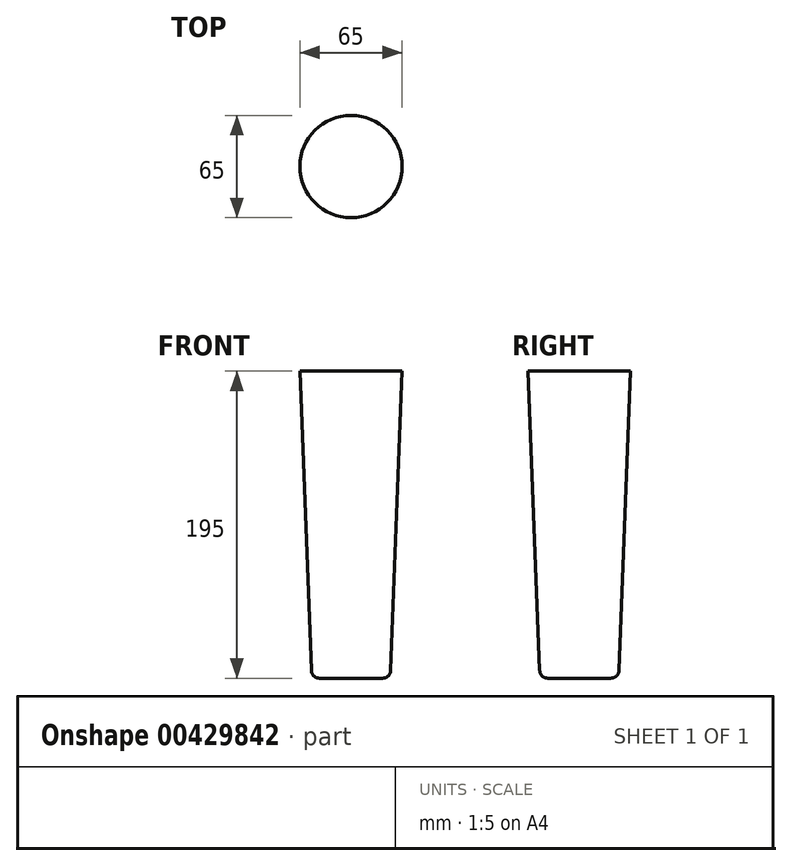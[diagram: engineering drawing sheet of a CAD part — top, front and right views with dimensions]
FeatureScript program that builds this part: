
annotation { "Feature Type Name" : "Feature", "Feature Type Description" : "" }
export const myFeature = defineFeature(function(context is Context, id is Id, definition is map)
    precondition{}
    {
        {
            var Q0;
            Q0=qCreatedBy(makeId("Top.planeOp"),FACE);
            var sketch = newSketch(context, id + "F0", { "sketchPlane" : qUnion([Q0])});
            skCircle(sketch, "E0", {"center": v(0, 0) * mm, "radius": 25 * mm});
            skSolve(sketch);
        }
        {
            var Q0;
            Q0=qCreatedBy(makeId("Top.planeOp"),FACE);
            cPlane(context, id + "F1", {"entities" : qUnion([Q0]), "cplaneType" : CPlaneType.OFFSET, "offset" : 195 * mm, "width" : 150 * mm, "height" : 150 * mm});
        }
        {
            var Q0;
            Q0=qCreatedBy(id+"F1.planeOp",FACE);
            var sketch = newSketch(context, id + "F2", { "sketchPlane" : qUnion([Q0])});
            skCircle(sketch, "E1", {"center": v(0, 0) * mm, "radius": 32.5 * mm});
            skSolve(sketch);
        }
        {
            var Q0;
            Q0=makeQuery(id+"F0.imprint","IMPRINT",FACE,{"disambiguationData":[TD([[makeQuery(id+"F0.imprint","IMPRINT",EDGE,{"derivedFrom":sQuery(id+"F0.wireOp",EDGE,"E0")}),1.0]])]});
            var Q1;
            Q1=makeQuery(id+"F2.imprint","IMPRINT",FACE,{"disambiguationData":[TD([[makeQuery(id+"F2.imprint","IMPRINT",EDGE,{"derivedFrom":sQuery(id+"F2.wireOp",EDGE,"E1")}),1.0]])]});
            loft(context, id + "F3", {"sheetProfilesArray" : [{ "sheetProfileEntities" : qUnion([Q0]) }, { "sheetProfileEntities" : qUnion([Q1]) }]});
        }
        {
            var Q0;
            Q0=makeQuery(id+"F3.opLoft","MID_CAP_EDGE",EDGE,{"disambiguationData":[OSD([sQuery(id+"F0.wireOp",EDGE,"E0")])],"capPos":0.0});
            fillet(context, id + "F4", {"entities" : qUnion([Q0]), "radius" : 5 * mm, "tangentPropagation" : true, "allowEdgeOverflow" : false});
        }
    });
